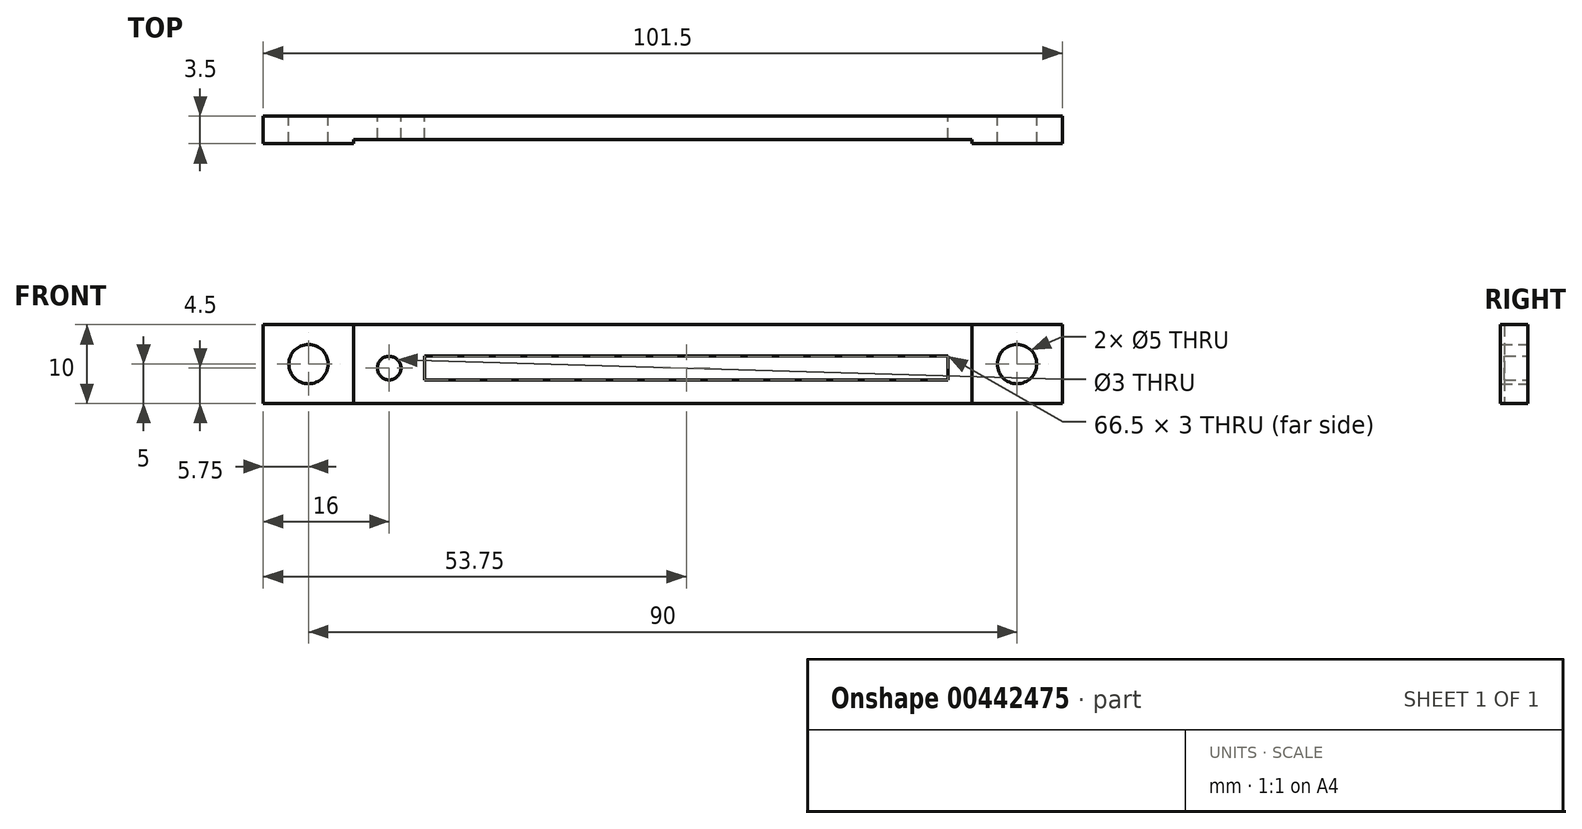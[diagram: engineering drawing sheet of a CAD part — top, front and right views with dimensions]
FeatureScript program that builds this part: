
annotation { "Feature Type Name" : "Feature", "Feature Type Description" : "" }
export const myFeature = defineFeature(function(context is Context, id is Id, definition is map)
    precondition{}
    {
        {
            var Q0;
            Q0=qCreatedBy(makeId("Front.planeOp"),FACE);
            var sketch = newSketch(context, id + "F0", { "sketchPlane" : qUnion([Q0])});
            skLineSegment(sketch, "E0.bottom", {"start": v(50.75, 5) * mm, "end": v(-50.75, 5) * mm});
            skLineSegment(sketch, "E0.top", {"start": v(50.75, -5) * mm, "end": v(-50.75, -5) * mm});
            skLineSegment(sketch, "E0.left", {"start": v(50.75, 5) * mm, "end": v(50.75, -5) * mm});
            skLineSegment(sketch, "E0.right", {"start": v(-50.75, 5) * mm, "end": v(-50.75, -5) * mm});
            skPoint(sketch, "E0.middle", {"position": v(0, 0) * mm});
            skLineSegment(sketch, "E1.bottom", {"start": v(39.25, 5) * mm, "end": v(-39.25, 5) * mm, "construction": true});
            skLineSegment(sketch, "E1.top", {"start": v(39.25, -5) * mm, "end": v(-39.25, -5) * mm, "construction": true});
            skLineSegment(sketch, "E1.left", {"start": v(39.25, 5) * mm, "end": v(39.25, -5) * mm, "construction": true});
            skLineSegment(sketch, "E1.right", {"start": v(-39.25, 5) * mm, "end": v(-39.25, -5) * mm, "construction": true});
            skLineSegment(sketch, "E2", {"start": v(50.75, 5) * mm, "end": v(39.25, -5) * mm, "construction": true});
            skLineSegment(sketch, "E3", {"start": v(39.25, 5) * mm, "end": v(50.75, -5) * mm, "construction": true});
            skLineSegment(sketch, "E4", {"start": v(-39.25, -5) * mm, "end": v(-50.75, 5) * mm, "construction": true});
            skLineSegment(sketch, "E5", {"start": v(-39.25, 5) * mm, "end": v(-50.75, -5) * mm, "construction": true});
            skCircle(sketch, "E6", {"center": v(-45, 0) * mm, "radius": 2.5 * mm});
            skCircle(sketch, "E7", {"center": v(45, 0) * mm, "radius": 2.5 * mm});
            skLineSegment(sketch, "E8.bottom", {"start": v(36.25, -2) * mm, "end": v(-30.25, -2) * mm});
            skLineSegment(sketch, "E8.top", {"start": v(36.25, 1) * mm, "end": v(-30.25, 1) * mm});
            skLineSegment(sketch, "E8.left", {"start": v(36.25, -2) * mm, "end": v(36.25, 1) * mm});
            skLineSegment(sketch, "E8.right", {"start": v(-30.25, -2) * mm, "end": v(-30.25, 1) * mm});
            skCircle(sketch, "E9", {"center": v(-34.75, -0.5) * mm, "radius": 1.5 * mm});
            skSolve(sketch);
        }
        {
            var Q0;
            Q0=qSketchRegion(id+"F0",true);
            extrude(context, id + "F1", {"entities" : qUnion([Q0]), "depth" : 3.5 * mm});
        }
        {
            var Q0;
            Q0=makeQuery(id+"F1.opExtrude","CAP_FACE",FACE,{"disambiguationData":[OSD([sQuery(id+"F0.wireOp",EDGE,"E0.bottom"),sQuery(id+"F0.wireOp",EDGE,"E0.top"),sQuery(id+"F0.wireOp",EDGE,"E0.left"),sQuery(id+"F0.wireOp",EDGE,"E0.right"),sQuery(id+"F0.wireOp",EDGE,"E6"),sQuery(id+"F0.wireOp",EDGE,"E7"),sQuery(id+"F0.wireOp",EDGE,"E8.bottom"),sQuery(id+"F0.wireOp",EDGE,"E8.top"),sQuery(id+"F0.wireOp",EDGE,"E8.left"),sQuery(id+"F0.wireOp",EDGE,"E8.right"),sQuery(id+"F0.wireOp",EDGE,"E9")])],"isStart":false});
            var sketch = newSketch(context, id + "F2", { "sketchPlane" : qUnion([Q0])});
            skLineSegment(sketch, "E10.bottom", {"start": v(39.25, 5) * mm, "end": v(-39.25, 5) * mm});
            skLineSegment(sketch, "E10.top", {"start": v(39.25, -5) * mm, "end": v(-39.25, -5) * mm});
            skLineSegment(sketch, "E10.left", {"start": v(39.25, 5) * mm, "end": v(39.25, -5) * mm});
            skLineSegment(sketch, "E10.right", {"start": v(-39.25, 5) * mm, "end": v(-39.25, -5) * mm});
            skPoint(sketch, "E10.middle", {"position": v(0, 0) * mm});
            skSolve(sketch);
        }
        {
            var Q0;
            Q0 = qSketchRegion(id + "F2", true);
            extrude(context, id + "F3", {"entities" : qUnion([Q0]), "operationType" : NewBodyOperationType.REMOVE, "oppositeDirection" : true, "depth" : .5 * mm});
        }
    });
